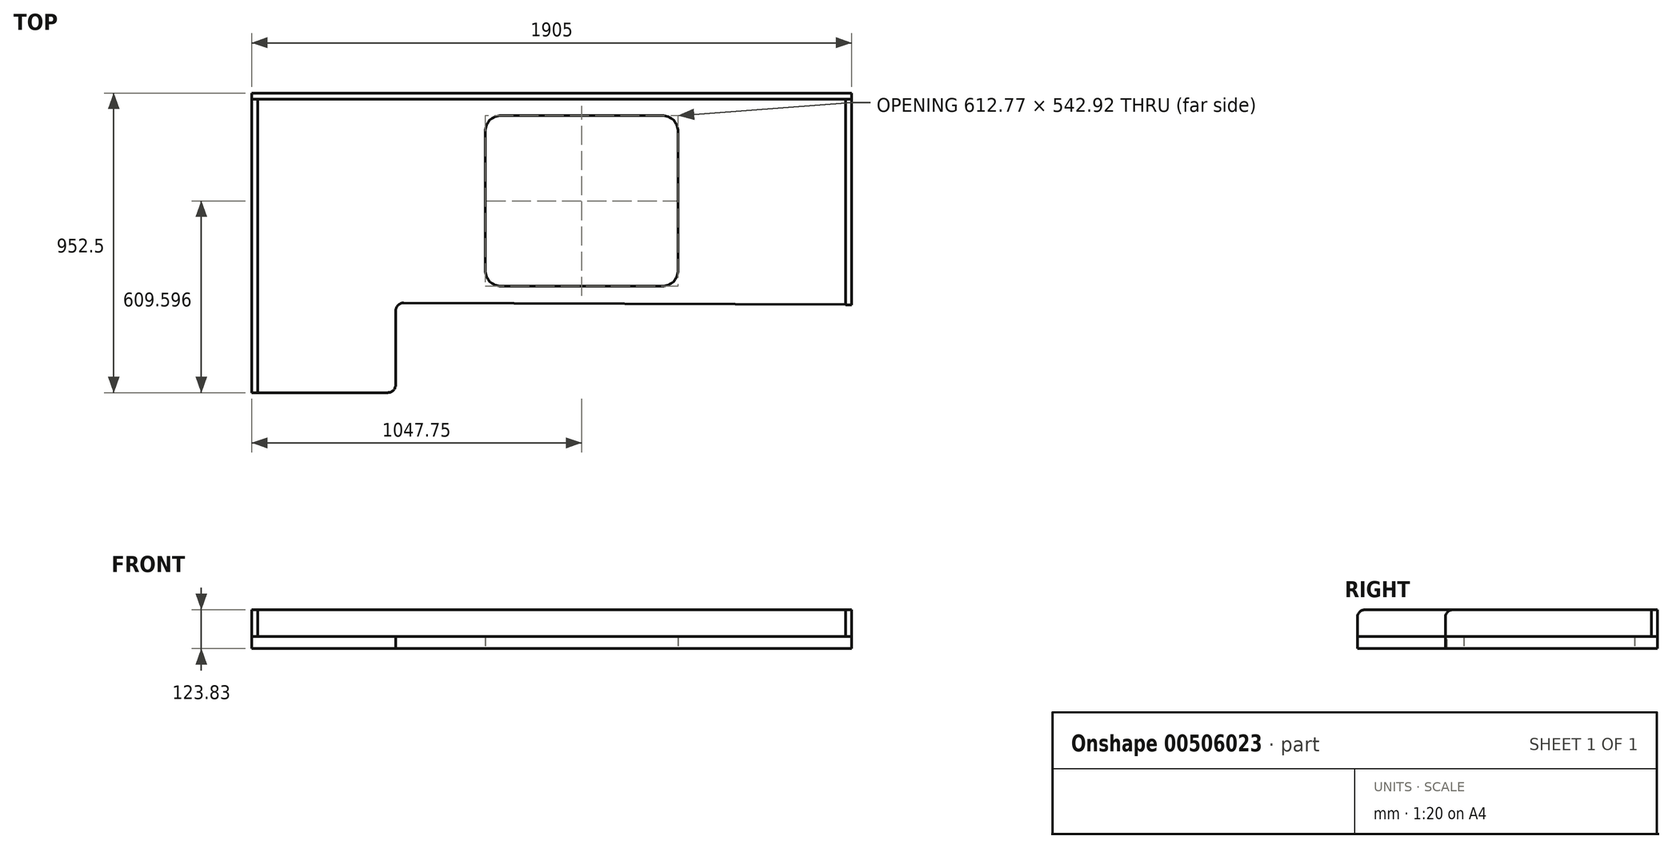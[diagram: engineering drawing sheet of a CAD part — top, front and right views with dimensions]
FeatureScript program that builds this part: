
annotation { "Feature Type Name" : "Feature", "Feature Type Description" : "" }
export const myFeature = defineFeature(function(context is Context, id is Id, definition is map)
    precondition{}
    {
        {
            var Q0;
            Q0=qCreatedBy(makeId("Top.planeOp"),FACE);
            var sketch = newSketch(context, id + "F0", { "sketchPlane" : qUnion([Q0])});
            skLineSegment(sketch, "E0.bottom", {"start": v(-703.98, 677.69) * mm, "end": v(1201.02, 677.69) * mm});
            skLineSegment(sketch, "E0.top", {"start": v(-703.98, -274.81) * mm, "end": v(-246.78, -274.81) * mm});
            skLineSegment(sketch, "E0.left", {"start": v(-703.98, 677.69) * mm, "end": v(-703.98, -274.81) * mm});
            skLineSegment(sketch, "E0.right", {"start": v(1201.02, 677.69) * mm, "end": v(1201.02, 4.59) * mm});
            skLineSegment(sketch, "E1", {"start": v(-246.78, -274.81) * mm, "end": v(-246.78, 10.63) * mm});
            skLineSegment(sketch, "E2", {"start": v(-246.78, 10.63) * mm, "end": v(1201.02, 4.59) * mm});
            skPoint(sketch, "E3.start.orphan", {"position": v(2300.42, 0) * mm});
            skLineSegment(sketch, "E4", {"start": v(55.37, 334.79) * mm, "end": v(808.2, 334.79) * mm, "construction": true});
            skLineSegment(sketch, "E5", {"start": v(343.77, 808.2) * mm, "end": v(343.77, 68.8) * mm, "construction": true});
            skLineSegment(sketch, "E6.bottom", {"start": v(37.38, 606.25) * mm, "end": v(650.15, 606.25) * mm});
            skLineSegment(sketch, "E6.top", {"start": v(37.38, 63.32) * mm, "end": v(650.15, 63.32) * mm});
            skLineSegment(sketch, "E6.left", {"start": v(37.38, 606.25) * mm, "end": v(37.38, 63.32) * mm});
            skLineSegment(sketch, "E6.right", {"start": v(650.15, 606.25) * mm, "end": v(650.15, 63.32) * mm});
            skSolve(sketch);
        }
        {
            var Q0;
            Q0 = qSketchRegion(id + "F0", true);
            extrude(context, id + "F1", {"entities" : qUnion([Q0]), "depth" : 38.1 * mm, "offsetDistance" : 25.4 * mm});
        }
        {
            var Q0;
            Q0=makeQuery(id+"F1.opExtrude","SWEPT_FACE",FACE,{"disambiguationData":[OSD([sQuery(id+"F0.wireOp",EDGE,"E0.left")])]});
            cPlane(context, id + "F2", {"entities" : qUnion([Q0]), "cplaneType" : CPlaneType.OFFSET, "offset" : 0 * mm, "width" : 152.4 * mm, "height" : 152.4 * mm});
        }
        {
            var Q0;
            Q0=qCreatedBy(id+"F2.planeOp",FACE);
            var sketch = newSketch(context, id + "F3", { "sketchPlane" : qUnion([Q0])});
            skLineSegment(sketch, "E7.bottom", {"start": v(-658.64, 123.83) * mm, "end": v(274.81, 123.83) * mm});
            skLineSegment(sketch, "E7.top", {"start": v(-658.64, 38.1) * mm, "end": v(274.81, 38.1) * mm});
            skLineSegment(sketch, "E7.left", {"start": v(-658.64, 123.83) * mm, "end": v(-658.64, 38.1) * mm});
            skLineSegment(sketch, "E7.right", {"start": v(274.81, 123.83) * mm, "end": v(274.81, 38.1) * mm});
            skSolve(sketch);
        }
        {
            var Q0;
            Q0 = qSketchRegion(id + "F3", true);
            extrude(context, id + "F4", {"entities" : qUnion([Q0]), "oppositeDirection" : true, "depth" : 19.05 * mm, "offsetDistance" : 25.4 * mm});
        }
        {
            var Q0;
            Q0=makeQuery(id+"F1.opExtrude","SWEPT_FACE",FACE,{"disambiguationData":[OSD([sQuery(id+"F0.wireOp",EDGE,"E0.right")])]});
            cPlane(context, id + "F5", {"entities" : qUnion([Q0]), "cplaneType" : CPlaneType.OFFSET, "offset" : 0 * mm, "width" : 152.4 * mm, "height" : 152.4 * mm});
        }
        {
            var Q0;
            Q0=qCreatedBy(id+"F5.planeOp",FACE);
            var sketch = newSketch(context, id + "F6", { "sketchPlane" : qUnion([Q0])});
            skLineSegment(sketch, "E8.bottom", {"start": v(4.59, 123.83) * mm, "end": v(658.64, 123.83) * mm});
            skLineSegment(sketch, "E8.top", {"start": v(4.59, 38.1) * mm, "end": v(658.64, 38.1) * mm});
            skLineSegment(sketch, "E8.left", {"start": v(4.59, 123.83) * mm, "end": v(4.59, 38.1) * mm});
            skLineSegment(sketch, "E8.right", {"start": v(658.64, 123.83) * mm, "end": v(658.64, 38.1) * mm});
            skSolve(sketch);
        }
        {
            var Q0;
            Q0 = qSketchRegion(id + "F6", true);
            extrude(context, id + "F7", {"entities" : qUnion([Q0]), "oppositeDirection" : true, "depth" : 19.05 * mm, "offsetDistance" : 25.4 * mm});
        }
        {
            var Q0;
            Q0=makeQuery(id+"F1.opExtrude","SWEPT_FACE",FACE,{"disambiguationData":[OSD([sQuery(id+"F0.wireOp",EDGE,"E0.bottom")])]});
            cPlane(context, id + "F8", {"entities" : qUnion([Q0]), "cplaneType" : CPlaneType.OFFSET, "offset" : 0 * mm, "width" : 152.4 * mm, "height" : 152.4 * mm});
        }
        {
            var Q0;
            Q0=qCreatedBy(id+"F8.planeOp",FACE);
            var sketch = newSketch(context, id + "F9", { "sketchPlane" : qUnion([Q0])});
            skLineSegment(sketch, "E9.bottom", {"start": v(-1201.02, 123.83) * mm, "end": v(703.98, 123.83) * mm});
            skLineSegment(sketch, "E9.top", {"start": v(-1201.02, 38.1) * mm, "end": v(703.98, 38.1) * mm});
            skLineSegment(sketch, "E9.left", {"start": v(-1201.02, 123.83) * mm, "end": v(-1201.02, 38.1) * mm});
            skLineSegment(sketch, "E9.right", {"start": v(703.98, 123.83) * mm, "end": v(703.98, 38.1) * mm});
            skSolve(sketch);
        }
        {
            var Q0;
            Q0 = qSketchRegion(id + "F9", true);
            extrude(context, id + "F10", {"entities" : qUnion([Q0]), "oppositeDirection" : true, "depth" : 19.05 * mm, "offsetDistance" : 25.4 * mm});
        }
        {
            var Q0;
            Q0=makeQuery(id+"F7.opExtrude","SWEPT_EDGE",EDGE,{"disambiguationData":[OSD([sQuery(id+"F6.wireOp",EDGE,"E8.bottom"),sQuery(id+"F6.wireOp",EDGE,"E8.left")])]});
            var Q1;
            Q1=makeQuery(id+"F4.opExtrude","SWEPT_EDGE",EDGE,{"disambiguationData":[OSD([sQuery(id+"F3.wireOp",EDGE,"E7.bottom"),sQuery(id+"F3.wireOp",EDGE,"E7.right")])]});
            fillet(context, id + "F11", {"entities" : qUnion([Q0, Q1]), "radius" : 25.4 * mm, "tangentPropagation" : true, "allowEdgeOverflow" : false});
        }
        {
            var Q0;
            Q0=makeQuery(id+"F1.opExtrude","SWEPT_EDGE",EDGE,{"disambiguationData":[OSD([sQuery(id+"F0.wireOp",EDGE,"E6.bottom"),sQuery(id+"F0.wireOp",EDGE,"E6.left")])]});
            var Q1;
            Q1=makeQuery(id+"F1.opExtrude","SWEPT_EDGE",EDGE,{"disambiguationData":[OSD([sQuery(id+"F0.wireOp",EDGE,"E6.bottom"),sQuery(id+"F0.wireOp",EDGE,"E6.right")])]});
            var Q2;
            Q2=makeQuery(id+"F1.opExtrude","SWEPT_EDGE",EDGE,{"disambiguationData":[OSD([sQuery(id+"F0.wireOp",EDGE,"E6.top"),sQuery(id+"F0.wireOp",EDGE,"E6.right")])]});
            var Q3;
            Q3=makeQuery(id+"F1.opExtrude","SWEPT_EDGE",EDGE,{"disambiguationData":[OSD([sQuery(id+"F0.wireOp",EDGE,"E6.top"),sQuery(id+"F0.wireOp",EDGE,"E6.left")])]});
            fillet(context, id + "F12", {"entities" : qUnion([Q0, Q1, Q2, Q3]), "radius" : 50.8 * mm, "tangentPropagation" : true, "allowEdgeOverflow" : false});
        }
        {
            var Q0;
            Q0=makeQuery(id+"F1.opExtrude","SWEPT_EDGE",EDGE,{"disambiguationData":[OSD([sQuery(id+"F0.wireOp",EDGE,"E0.top"),sQuery(id+"F0.wireOp",EDGE,"E1")])]});
            var Q1;
            Q1=makeQuery(id+"F1.opExtrude","SWEPT_EDGE",EDGE,{"disambiguationData":[OSD([sQuery(id+"F0.wireOp",EDGE,"E1"),sQuery(id+"F0.wireOp",EDGE,"E2")])]});
            fillet(context, id + "F13", {"entities" : qUnion([Q0, Q1]), "radius" : 25.4 * mm, "tangentPropagation" : true, "allowEdgeOverflow" : false});
        }
    });
